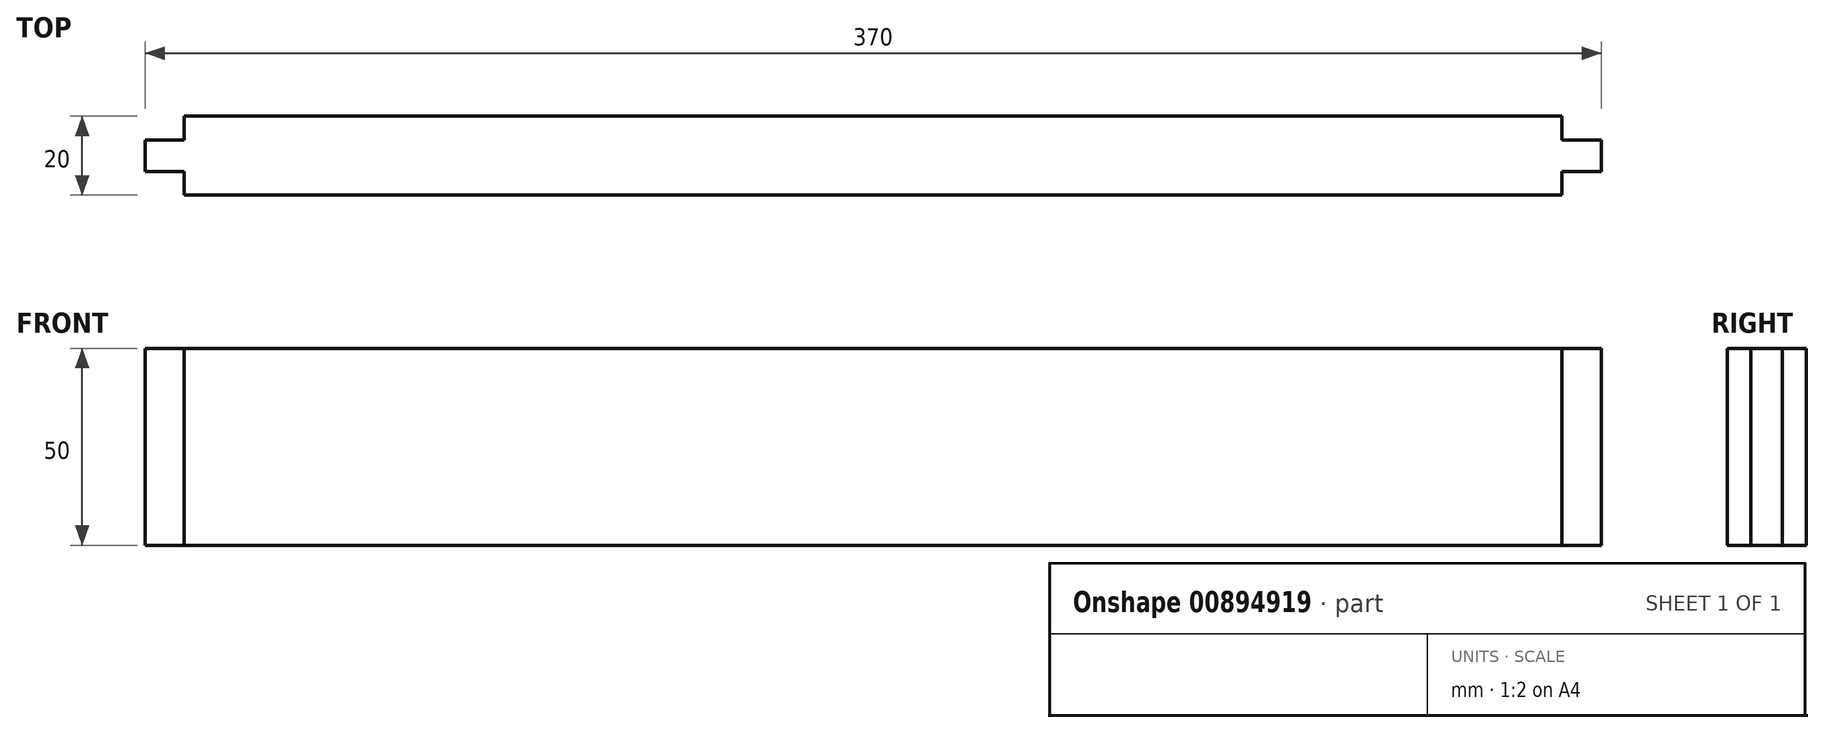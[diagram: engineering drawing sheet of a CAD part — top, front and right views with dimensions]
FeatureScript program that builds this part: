
annotation { "Feature Type Name" : "Feature", "Feature Type Description" : "" }
export const myFeature = defineFeature(function(context is Context, id is Id, definition is map)
    precondition{}
    {
        {
            var Q0;
            Q0=qCreatedBy(makeId("Front.planeOp"),FACE);
            var sketch = newSketch(context, id + "F0", { "sketchPlane" : qUnion([Q0])});
            skLineSegment(sketch, "E0.bottom", {"start": v(-372.51, 72.09) * mm, "end": v(-22.51, 72.09) * mm});
            skLineSegment(sketch, "E0.top", {"start": v(-372.51, 22.09) * mm, "end": v(-22.51, 22.09) * mm});
            skLineSegment(sketch, "E0.left", {"start": v(-372.51, 72.09) * mm, "end": v(-372.51, 22.09) * mm});
            skLineSegment(sketch, "E0.right", {"start": v(-22.51, 72.09) * mm, "end": v(-22.51, 22.09) * mm});
            skSolve(sketch);
        }
        {
            var Q0;
            Q0=makeQuery(id+"F0.imprint","IMPRINT",FACE,{"disambiguationData":[TD([[makeQuery(id+"F0.imprint","IMPRINT",EDGE,{"derivedFrom":sQuery(id+"F0.wireOp",EDGE,"E0.bottom")}),-1.0]])]});
            extrude(context, id + "F1", {"entities" : qUnion([Q0]), "depth" : 20 * mm, "offsetDistance" : 25 * mm});
        }
        {
            var Q0;
            Q0=makeQuery(id+"F1.opExtrude","SWEPT_FACE",FACE,{"disambiguationData":[OSD([sQuery(id+"F0.wireOp",EDGE,"E0.right")])]});
            var sketch = newSketch(context, id + "F2", { "sketchPlane" : qUnion([Q0])});
            skLineSegment(sketch, "E1.bottom", {"start": v(-14, 72.09) * mm, "end": v(-6, 72.09) * mm});
            skLineSegment(sketch, "E1.top", {"start": v(-14, 22.09) * mm, "end": v(-6, 22.09) * mm});
            skLineSegment(sketch, "E1.left", {"start": v(-14, 72.09) * mm, "end": v(-14, 22.09) * mm});
            skLineSegment(sketch, "E1.right", {"start": v(-6, 72.09) * mm, "end": v(-6, 22.09) * mm});
            skPoint(sketch, "E1.middle", {"position": v(-10, 47.09) * mm});
            skPoint(sketch, "E1.middle.positionSnap0", {"position": v(0, 47.09) * mm});
            skPoint(sketch, "E1.centerSnap0", {"position": v(0, 47.09) * mm});
            skSolve(sketch);
        }
        {
            var Q0;
            Q0=makeQuery(id+"F2.imprint","IMPRINT",FACE,{"disambiguationData":[TD([[makeQuery(id+"F2.imprint","IMPRINT",EDGE,{"derivedFrom":sQuery(id+"F2.wireOp",EDGE,"E1.bottom")}),-1.0]])]});
            extrude(context, id + "F3", {"entities" : qUnion([Q0]), "operationType" : NewBodyOperationType.ADD, "depth" : 10 * mm, "offsetDistance" : 25 * mm});
        }
        {
            var Q0;
            Q0=makeQuery(id+"F1.opExtrude","SWEPT_FACE",FACE,{"disambiguationData":[OSD([sQuery(id+"F0.wireOp",EDGE,"E0.left")])]});
            var sketch = newSketch(context, id + "F4", { "sketchPlane" : qUnion([Q0])});
            skLineSegment(sketch, "E2.bottom", {"start": v(14, 22.09) * mm, "end": v(6, 22.09) * mm});
            skLineSegment(sketch, "E2.top", {"start": v(14, 72.09) * mm, "end": v(6, 72.09) * mm});
            skLineSegment(sketch, "E2.left", {"start": v(14, 22.09) * mm, "end": v(14, 72.09) * mm});
            skLineSegment(sketch, "E2.right", {"start": v(6, 22.09) * mm, "end": v(6, 72.09) * mm});
            skPoint(sketch, "E2.middle", {"position": v(10, 47.09) * mm});
            skPoint(sketch, "E2.middle.positionSnap0", {"position": v(20, 47.09) * mm});
            skPoint(sketch, "E2.centerSnap0", {"position": v(20, 47.09) * mm});
            skSolve(sketch);
        }
        {
            var Q0;
            Q0=makeQuery(id+"F4.imprint","IMPRINT",FACE,{"disambiguationData":[TD([[makeQuery(id+"F4.imprint","IMPRINT",EDGE,{"derivedFrom":sQuery(id+"F4.wireOp",EDGE,"E2.bottom")}),-1.0]])]});
            extrude(context, id + "F5", {"entities" : qUnion([Q0]), "operationType" : NewBodyOperationType.ADD, "depth" : 10 * mm, "offsetDistance" : 25 * mm});
        }
    });
